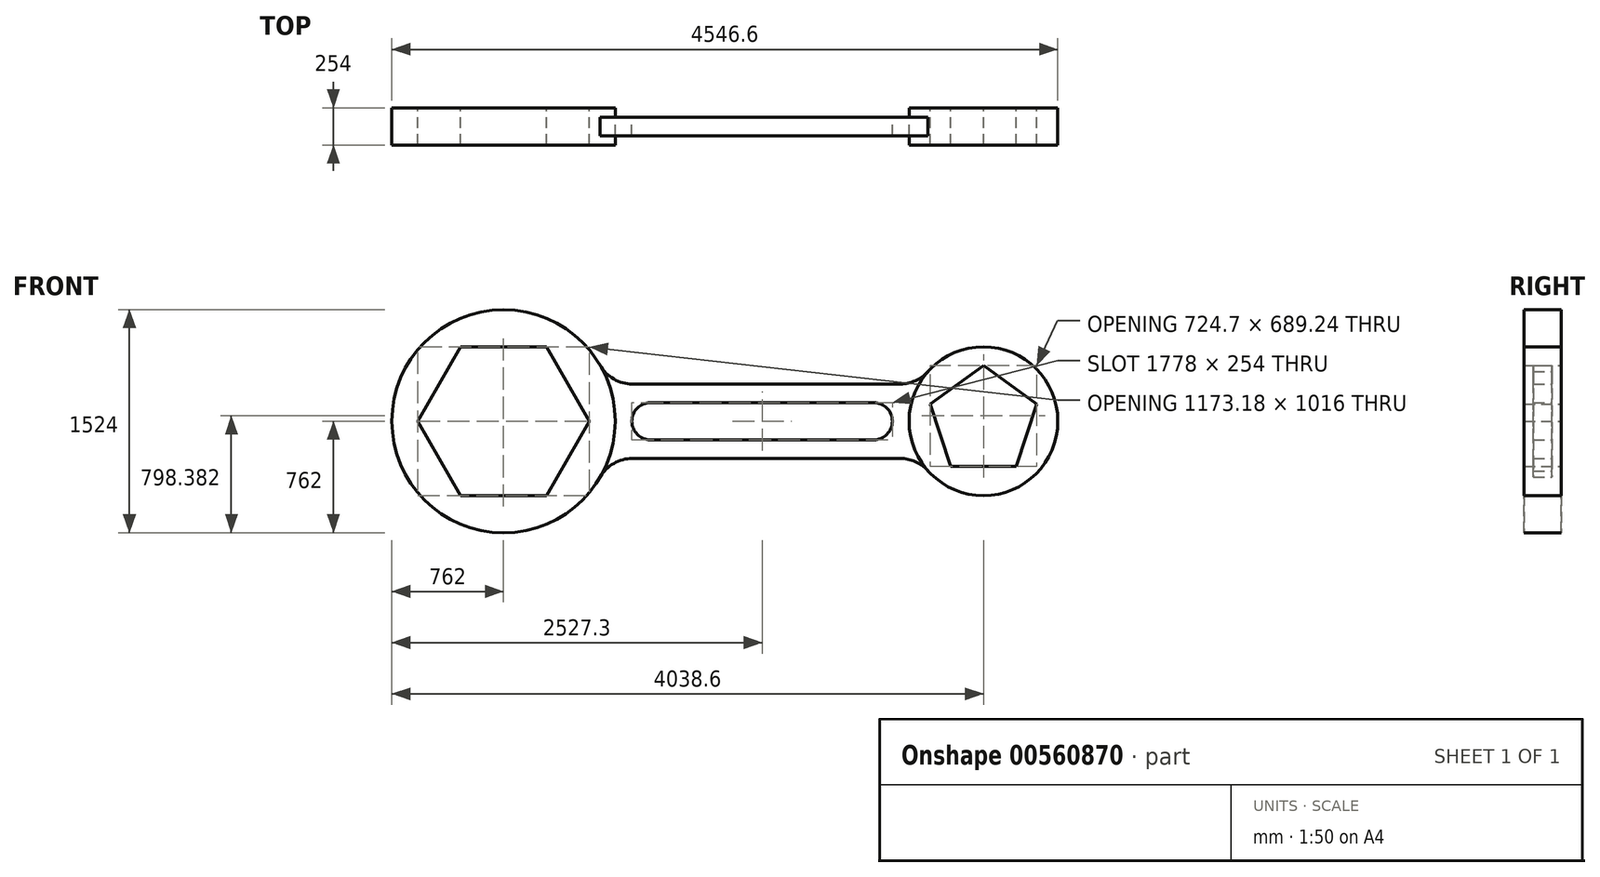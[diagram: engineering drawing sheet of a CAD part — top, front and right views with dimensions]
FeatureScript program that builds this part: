
annotation { "Feature Type Name" : "Feature", "Feature Type Description" : "" }
export const myFeature = defineFeature(function(context is Context, id is Id, definition is map)
    precondition{}
    {
        {
            var Q0;
            Q0=qCreatedBy(makeId("Front.planeOp"),FACE);
            var sketch = newSketch(context, id + "F0", { "sketchPlane" : qUnion([Q0])});
            skArc(sketch, "E0", {"start": v(659.91, 381) * mm, "mid": v(-762, 0) * mm, "end": v(659.91, -381) * mm});
            skArc(sketch, "E1", {"start": v(2897.96, -338.67) * mm, "mid": v(3784.6, 0) * mm, "end": v(2897.96, 338.67) * mm});
            skLineSegment(sketch, "E2", {"start": v(1765.3, 127) * mm, "end": v(1003.3, 127) * mm});
            skLineSegment(sketch, "E3", {"start": v(2527.3, 127) * mm, "end": v(1765.3, 127) * mm});
            skArc(sketch, "E4", {"start": v(1003.3, 127) * mm, "mid": v(876.3, 0) * mm, "end": v(1003.3, -127) * mm});
            skArc(sketch, "E5", {"start": v(2527.3, -127) * mm, "mid": v(2654.3, 0) * mm, "end": v(2527.3, 127) * mm});
            skPoint(sketch, "E6.orphan", {"position": v(2654.3, 127) * mm});
            skPoint(sketch, "E7.orphan", {"position": v(2654.3, -127) * mm});
            skPoint(sketch, "E8.start.orphan", {"position": v(2654.3, 0) * mm});
            skPoint(sketch, "E9.orphan", {"position": v(876.3, 127) * mm});
            skPoint(sketch, "E10.orphan", {"position": v(876.3, -127) * mm});
            skPoint(sketch, "E11.start.orphan", {"position": v(876.3, 0) * mm});
            skPoint(sketch, "E12.start.orphan", {"position": v(1765.3, 0) * mm});
            skLineSegment(sketch, "E13", {"start": v(879.88, 254) * mm, "end": v(2708.64, 254) * mm});
            skLineSegment(sketch, "E14", {"start": v(879.88, -254) * mm, "end": v(2708.64, -254) * mm});
            skArc(sketch, "E15", {"start": v(659.91, 381) * mm, "mid": v(752.88, 288.03) * mm, "end": v(879.88, 254) * mm});
            skArc(sketch, "E16", {"start": v(2708.64, 254) * mm, "mid": v(2812.33, 276.13) * mm, "end": v(2897.96, 338.67) * mm});
            skArc(sketch, "E17", {"start": v(879.88, -254) * mm, "mid": v(752.88, -288.03) * mm, "end": v(659.91, -381) * mm});
            skPoint(sketch, "E18.orphan", {"position": v(762, 0) * mm});
            skPoint(sketch, "E19.orphan", {"position": v(2768.6, 0) * mm});
            skArc(sketch, "E20", {"start": v(2897.96, -338.67) * mm, "mid": v(2812.33, -276.13) * mm, "end": v(2708.64, -254) * mm});
            skLineSegment(sketch, "E21.0", {"start": v(3500.55, -308.24) * mm, "end": v(3052.65, -308.24) * mm});
            skLineSegment(sketch, "E21.1", {"start": v(3052.65, -308.24) * mm, "end": v(2914.25, 117.74) * mm});
            skLineSegment(sketch, "E21.2", {"start": v(2914.25, 117.74) * mm, "end": v(3276.6, 381) * mm});
            skLineSegment(sketch, "E21.3", {"start": v(3276.6, 381) * mm, "end": v(3638.95, 117.74) * mm});
            skLineSegment(sketch, "E21.4", {"start": v(3638.95, 117.74) * mm, "end": v(3500.55, -308.24) * mm});
            skPoint(sketch, "E21.0.midPoint", {"position": v(3276.6, -308.24) * mm});
            skLineSegment(sketch, "E22.0", {"start": v(-293.3, 508) * mm, "end": v(293.3, 508) * mm});
            skLineSegment(sketch, "E22.1", {"start": v(293.3, 508) * mm, "end": v(586.59, 0) * mm});
            skLineSegment(sketch, "E22.2", {"start": v(586.59, 0) * mm, "end": v(293.3, -508) * mm});
            skLineSegment(sketch, "E22.3", {"start": v(293.3, -508) * mm, "end": v(-293.3, -508) * mm});
            skLineSegment(sketch, "E22.4", {"start": v(-293.3, -508) * mm, "end": v(-586.59, 0) * mm});
            skLineSegment(sketch, "E22.5", {"start": v(-586.59, 0) * mm, "end": v(-293.3, 508) * mm});
            skPoint(sketch, "E22.0.midPoint", {"position": v(0, 508) * mm});
            skLineSegment(sketch, "E23", {"start": v(1003.3, -127) * mm, "end": v(2527.3, -127) * mm});
            skArc(sketch, "E24", {"start": v(659.91, -381) * mm, "mid": v(762, 0) * mm, "end": v(659.91, 381) * mm});
            skArc(sketch, "E25", {"start": v(2897.96, 338.67) * mm, "mid": v(2768.6, 0) * mm, "end": v(2897.96, -338.67) * mm});
            skSolve(sketch);
        }
        {
            var Q0;
            Q0=makeQuery(id+"F0.imprint","IMPRINT",FACE,{"disambiguationData":[TD([[makeQuery(id+"F0.imprint","IMPRINT",EDGE,{"derivedFrom":sQuery(id+"F0.wireOp",EDGE,"E0")}),1.0]])]});
            extrude(context, id + "F1", {"entities" : qUnion([Q0]), "depth" : 254 * mm, "offsetDistance" : 25.4 * mm, "symmetric" : true});
        }
        {
            var Q0;
            Q0=makeQuery(id+"F0.imprint","IMPRINT",FACE,{"disambiguationData":[TD([[makeQuery(id+"F0.imprint","IMPRINT",EDGE,{"derivedFrom":sQuery(id+"F0.wireOp",EDGE,"E1")}),1.0]])]});
            extrude(context, id + "F2", {"entities" : qUnion([Q0]), "depth" : 254 * mm, "offsetDistance" : 25.4 * mm, "symmetric" : true});
        }
        {
            var Q0;
            Q0=makeQuery(id+"F0.imprint","IMPRINT",FACE,{"disambiguationData":[TD([[makeQuery(id+"F0.imprint","IMPRINT",EDGE,{"derivedFrom":sQuery(id+"F0.wireOp",EDGE,"E2")}),-1.0]])]});
            extrude(context, id + "F3", {"entities" : qUnion([Q0]), "depth" : 127 * mm, "offsetDistance" : 25.4 * mm, "symmetric" : true});
        }
    });
